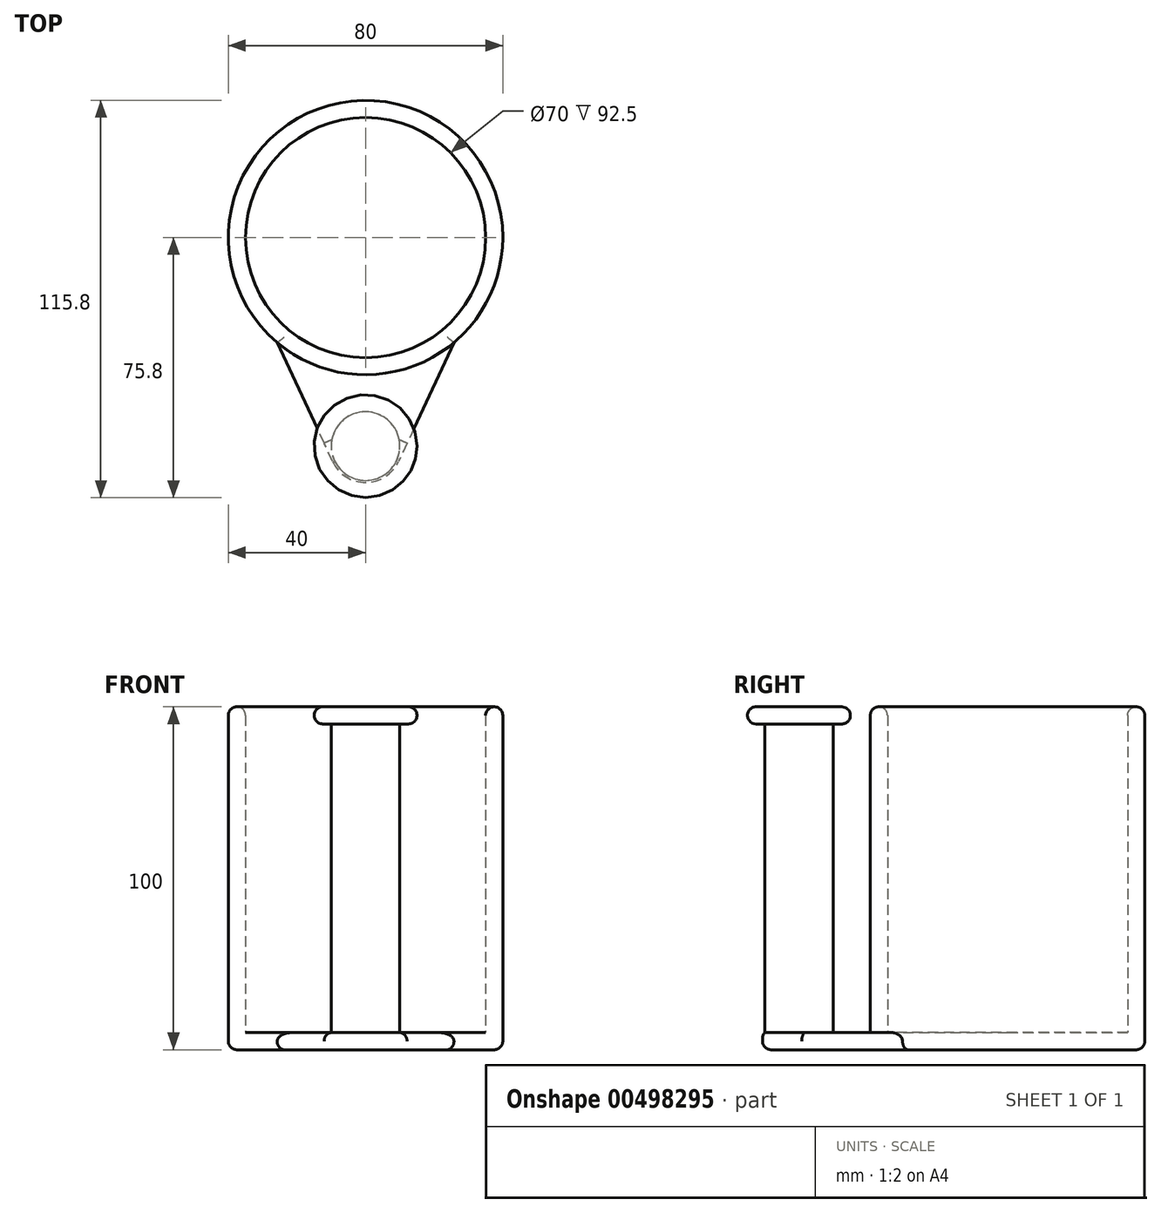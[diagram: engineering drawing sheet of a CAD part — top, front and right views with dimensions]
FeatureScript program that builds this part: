
annotation { "Feature Type Name" : "Feature", "Feature Type Description" : "" }
export const myFeature = defineFeature(function(context is Context, id is Id, definition is map)
    precondition{}
    {
        {
            var Q0;
            Q0=qCreatedBy(makeId("Top.planeOp"),FACE);
            var sketch = newSketch(context, id + "F0", { "sketchPlane" : qUnion([Q0])});
            skCircle(sketch, "E0", {"center": v(0, 0) * mm, "radius": 40 * mm});
            skSolve(sketch);
        }
        {
            var Q0;
            Q0 = qSketchRegion(id + "F0", true);
            extrude(context, id + "F1", {"entities" : qUnion([Q0]), "depth" : 100 * mm});
        }
        {
            var Q0;
            Q0=makeQuery(id+"F1.opExtrude","CAP_FACE",FACE,{"disambiguationData":[OSD([sQuery(id+"F0.wireOp",EDGE,"E0")])],"isStart":false});
            var Q1;
            Q1=makeQuery(id+"F1.opExtrude","SWEPT_BODY",BODY,{"disambiguationData":[OSD([sQuery(id+"F0.wireOp",EDGE,"E0")])]});
            shell(context, id + "F2", {"entities" : qUnion([Q0]), "parts" : qUnion([Q1]), "thickness" : 5 * mm});
        }
        {
            var Q0;
            Q0=qCreatedBy(makeId("Top.planeOp"),FACE);
            var sketch = newSketch(context, id + "F3", { "sketchPlane" : qUnion([Q0])});
            skLineSegment(sketch, "E1", {"start": v(40, 0) * mm, "end": v(0, 0) * mm});
            skLineSegment(sketch, "E2", {"start": v(0, 0) * mm, "end": v(-40, 0) * mm});
            skLineSegment(sketch, "E3", {"start": v(40, 0) * mm, "end": v(9.63, -65.28) * mm});
            skLineSegment(sketch, "E4", {"start": v(-9.62, -65.28) * mm, "end": v(-40, 0) * mm});
            skArc(sketch, "E5", {"start": v(-9.62, -65.28) * mm, "mid": v(0, -71.42) * mm, "end": v(9.63, -65.28) * mm});
            skSolve(sketch);
        }
        {
            var Q0;
            Q0 = qSketchRegion(id + "F3", true);
            extrude(context, id + "F4", {"entities" : qUnion([Q0]), "operationType" : NewBodyOperationType.ADD, "depth" : 5 * mm});
        }
        {
            var Q0;
            Q0=makeQuery(id+"F4.opExtrude","CAP_FACE",FACE,{"disambiguationData":[OSD([sQuery(id+"F3.wireOp",EDGE,"E1"),sQuery(id+"F3.wireOp",EDGE,"E2"),sQuery(id+"F3.wireOp",EDGE,"E3"),sQuery(id+"F3.wireOp",EDGE,"E4"),sQuery(id+"F3.wireOp",EDGE,"E5")])],"isStart":false});
            var sketch = newSketch(context, id + "F5", { "sketchPlane" : qUnion([Q0])});
            skCircle(sketch, "E6", {"center": v(0, -60.8) * mm, "radius": 10 * mm});
            skSolve(sketch);
        }
        {
            var Q0;
            Q0 = qSketchRegion(id + "F5", true);
            extrude(context, id + "F6", {"entities" : qUnion([Q0]), "operationType" : NewBodyOperationType.ADD, "depth" : 90 * mm});
        }
        {
            var Q0;
            Q0=makeQuery(id+"F6.opExtrude","CAP_FACE",FACE,{"disambiguationData":[OSD([sQuery(id+"F5.wireOp",EDGE,"E6")])],"isStart":false});
            var sketch = newSketch(context, id + "F7", { "sketchPlane" : qUnion([Q0])});
            skCircle(sketch, "E7", {"center": v(0, -60.8) * mm, "radius": 15 * mm});
            skSolve(sketch);
        }
        {
            var Q0;
            Q0 = qSketchRegion(id + "F7", true);
            extrude(context, id + "F8", {"entities" : qUnion([Q0]), "operationType" : NewBodyOperationType.ADD, "depth" : 5 * mm});
        }
        {
            var Q0;
            Q0=makeQuery(id+"F1.opExtrude","CAP_EDGE",EDGE,{"disambiguationData":[OSD([sQuery(id+"F0.wireOp",EDGE,"E0")])],"isStart":false});
            var Q1;
            {var subQ0=sQuery(id+"F0.wireOp",EDGE,"E0");Q1=makeQuery(id+"F2.opShell","OFFSET_EDGE",EDGE,{"disambiguationData":[OSD([subQ0]),TDD([makeQuery(id+"F1.opExtrude","CAP_EDGE",EDGE,{"disambiguationData":[OSD([subQ0])],"isStart":false})])]});}
            var Q2;
            Q2=makeQuery(id+"F1.opExtrude","CAP_EDGE",EDGE,{"disambiguationData":[OSD([sQuery(id+"F0.wireOp",EDGE,"E0")])],"isStart":true});
            var Q3;
            Q3=makeQuery(id+"F8.opExtrude","CAP_EDGE",EDGE,{"disambiguationData":[OSD([sQuery(id+"F7.wireOp",EDGE,"E7")])],"isStart":false});
            var Q4;
            Q4=makeQuery(id+"F8.opExtrude","CAP_EDGE",EDGE,{"disambiguationData":[OSD([sQuery(id+"F7.wireOp",EDGE,"E7")])],"isStart":true});
            var Q5;
            Q5=makeQuery(id+"F4.opExtrude","CAP_EDGE",EDGE,{"disambiguationData":[OSD([sQuery(id+"F3.wireOp",EDGE,"E4")])],"isStart":false});
            var Q6;
            Q6=makeQuery(id+"F4.opExtrude","CAP_EDGE",EDGE,{"disambiguationData":[OSD([sQuery(id+"F3.wireOp",EDGE,"E4")])],"isStart":true});
            var Q7;
            Q7=makeQuery(id+"F4.opExtrude","CAP_EDGE",EDGE,{"disambiguationData":[OSD([sQuery(id+"F3.wireOp",EDGE,"E5")])],"isStart":true});
            var Q8;
            Q8=makeQuery(id+"F4.opExtrude","CAP_EDGE",EDGE,{"disambiguationData":[OSD([sQuery(id+"F3.wireOp",EDGE,"E3")])],"isStart":false});
            var Q9;
            Q9=makeQuery(id+"F4.opExtrude","CAP_EDGE",EDGE,{"disambiguationData":[OSD([sQuery(id+"F3.wireOp",EDGE,"E3")])],"isStart":true});
            fillet(context, id + "F9", {"entities" : qUnion([Q0, Q1, Q2, Q3, Q4, Q5, Q6, Q7, Q8, Q9]), "radius" : 2.5 * mm, "tangentPropagation" : true, "allowEdgeOverflow" : false});
        }
    });
